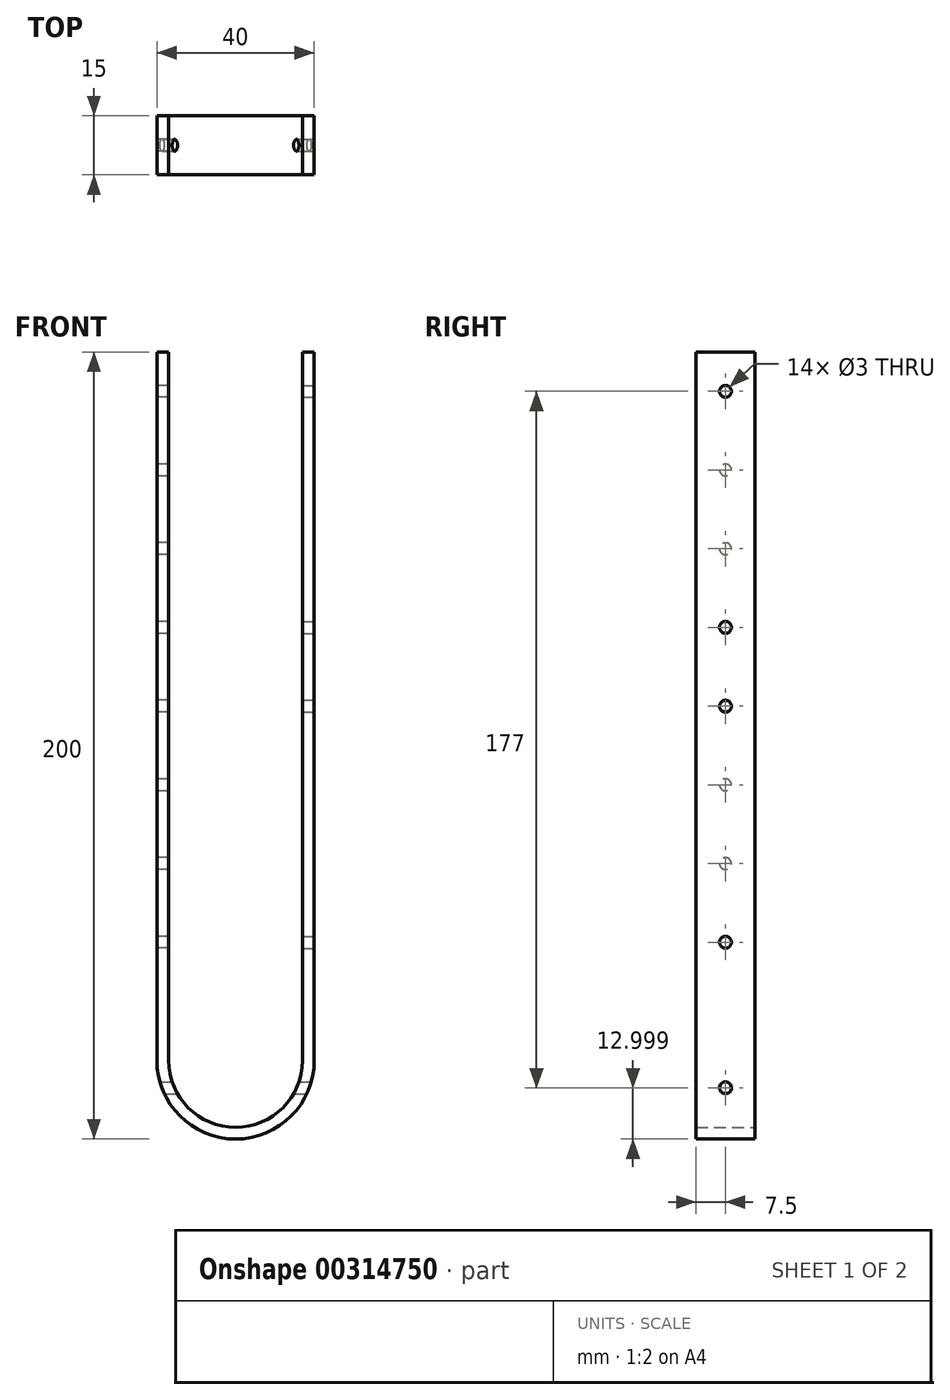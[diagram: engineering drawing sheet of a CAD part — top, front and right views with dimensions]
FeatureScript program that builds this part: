
annotation { "Feature Type Name" : "Feature", "Feature Type Description" : "" }
export const myFeature = defineFeature(function(context is Context, id is Id, definition is map)
    precondition{}
    {
        {
            var Q0;
            Q0=qCreatedBy(makeId("Front.planeOp"),FACE);
            var sketch = newSketch(context, id + "F0", { "sketchPlane" : qUnion([Q0])});
            skCircle(sketch, "E0", {"center": v(-118.34, -41.15) * mm, "radius": 20 * mm});
            skArc(sketch, "E1", {"start": v(-27.36, -89.87) * mm, "mid": v(-7.36, -109.87) * mm, "end": v(12.64, -89.87) * mm});
            skLineSegment(sketch, "E2", {"start": v(-27.36, -89.87) * mm, "end": v(-27.36, 90.13) * mm});
            skLineSegment(sketch, "E3", {"start": v(12.64, -89.87) * mm, "end": v(12.64, 90.13) * mm});
            skLineSegment(sketch, "E4.0", {"start": v(-24.36, -89.87) * mm, "end": v(-24.36, 90.13) * mm});
            skArc(sketch, "E4.1", {"start": v(-24.36, -89.87) * mm, "mid": v(-7.36, -106.87) * mm, "end": v(9.64, -89.87) * mm});
            skLineSegment(sketch, "E4.2", {"start": v(9.64, -89.87) * mm, "end": v(9.64, 90.13) * mm});
            skLineSegment(sketch, "E5", {"start": v(-27.36, 90.13) * mm, "end": v(-24.36, 90.13) * mm});
            skLineSegment(sketch, "E6", {"start": v(9.64, 90.13) * mm, "end": v(12.64, 90.13) * mm});
            skSolve(sketch);
        }
        {
            var Q0;
            Q0=makeQuery(id+"F0.imprint","IMPRINT",FACE,{"disambiguationData":[TD([[makeQuery(id+"F0.imprint","IMPRINT",EDGE,{"derivedFrom":sQuery(id+"F0.wireOp",EDGE,"E1")}),1.0]])]});
            extrude(context, id + "F1", {"entities" : qUnion([Q0]), "depth" : 15 * mm, "offsetDistance" : 25 * mm});
        }
        {
            var Q0;
            Q0=makeQuery(id+"F1.opExtrude","SWEPT_FACE",FACE,{"disambiguationData":[OSD([sQuery(id+"F0.wireOp",EDGE,"E2")])]});
            var sketch = newSketch(context, id + "F2", { "sketchPlane" : qUnion([Q0])});
            skLineSegment(sketch, "E7", {"start": v(7.5, 90.13) * mm, "end": v(7.5, 80.13) * mm});
            skCircle(sketch, "E8", {"center": v(7.5, 80.13) * mm, "radius": 1.5 * mm});
            skLineSegment(sketch, "E9", {"start": v(7.5, 80.13) * mm, "end": v(7.5, 60.13) * mm});
            skCircle(sketch, "E10", {"center": v(7.5, 60.13) * mm, "radius": 1.5 * mm});
            skLineSegment(sketch, "E11", {"start": v(7.5, 60.13) * mm, "end": v(7.5, 40.13) * mm});
            skCircle(sketch, "E12", {"center": v(7.5, 40.13) * mm, "radius": 1.5 * mm});
            skLineSegment(sketch, "E13", {"start": v(7.5, 40.13) * mm, "end": v(7.5, 90.13) * mm});
            skLineSegment(sketch, "E14.trimOffspring", {"start": v(7.5, 40.13) * mm, "end": v(7.5, 40.13) * mm});
            skPoint(sketch, "E15.start.orphan", {"position": v(7.5, -89.87) * mm});
            skLineSegment(sketch, "E16", {"start": v(7.5, 40.13) * mm, "end": v(7.5, 20.13) * mm});
            skCircle(sketch, "E17", {"center": v(7.5, 20.13) * mm, "radius": 1.35 * mm});
            skLineSegment(sketch, "E18", {"start": v(7.5, 20.13) * mm, "end": v(7.5, 0.13) * mm});
            skCircle(sketch, "E19", {"center": v(7.5, 0.13) * mm, "radius": 1.5 * mm});
            skLineSegment(sketch, "E20", {"start": v(7.5, 0.13) * mm, "end": v(7.5, -19.87) * mm});
            skCircle(sketch, "E21", {"center": v(7.5, -19.87) * mm, "radius": 1.5 * mm});
            skLineSegment(sketch, "E22", {"start": v(7.5, -19.87) * mm, "end": v(7.5, -39.87) * mm});
            skCircle(sketch, "E23", {"center": v(7.5, -39.87) * mm, "radius": 1.5 * mm});
            skLineSegment(sketch, "E24", {"start": v(7.5, -39.87) * mm, "end": v(7.5, -59.87) * mm});
            skCircle(sketch, "E25", {"center": v(7.5, -59.87) * mm, "radius": 1.5 * mm});
            skSolve(sketch);
        }
        {
            var Q0;
            Q0=sQuery(id+"F2.wireOp",VERTEX,"E9.start");
            var Q1;
            Q1=sQuery(id+"F2.wireOp",VERTEX,"E17.center");
            var Q2;
            Q2=sQuery(id+"F2.wireOp",VERTEX,"E20.start");
            var Q3;
            Q3=sQuery(id+"F2.wireOp",VERTEX,"E25.center");
            var Q4;
            Q4=sQuery(id+"F2.wireOp",VERTEX,"E11.start");
            var Q5;
            Q5=sQuery(id+"F2.wireOp",VERTEX,"E13.start");
            var Q6;
            Q6=sQuery(id+"F2.wireOp",VERTEX,"E22.start");
            var Q7;
            Q7=sQuery(id+"F2.wireOp",VERTEX,"E24.start");
            var Q8;
            Q8=makeQuery(id+"F1.opExtrude","SWEPT_BODY",BODY,{"disambiguationData":[OSD([sQuery(id+"F0.wireOp",EDGE,"E1"),sQuery(id+"F0.wireOp",EDGE,"E2"),sQuery(id+"F0.wireOp",EDGE,"E3"),sQuery(id+"F0.wireOp",EDGE,"E4.0"),sQuery(id+"F0.wireOp",EDGE,"E4.1"),sQuery(id+"F0.wireOp",EDGE,"E4.2"),sQuery(id+"F0.wireOp",EDGE,"E5"),sQuery(id+"F0.wireOp",EDGE,"E6")])]});
            hole(context, id + "F3", {"style" : HoleStyle.SIMPLE, "endStyle" : HoleEndStyle.BLIND, "holeDiameter" : 3 * mm, "holeDepth" : 10 * mm, "tappedDepth" : 12 * mm, "tapClearance" : 3, "locations" : qUnion([Q0, Q1, Q2, Q3, Q4, Q5, Q6, Q7]), "scope" : qUnion([Q8])});
        }
        {
            var Q0;
            Q0=makeQuery(id+"F1.opExtrude","SWEPT_FACE",FACE,{"disambiguationData":[OSD([sQuery(id+"F0.wireOp",EDGE,"E3")])]});
            var sketch = newSketch(context, id + "F4", { "sketchPlane" : qUnion([Q0])});
            skLineSegment(sketch, "E26", {"start": v(-7.5, 90.13) * mm, "end": v(-7.5, 80.13) * mm});
            skCircle(sketch, "E27", {"center": v(-7.5, 80.13) * mm, "radius": 1.5 * mm});
            skLineSegment(sketch, "E28", {"start": v(-7.5, 80.13) * mm, "end": v(-7.5, 20.13) * mm});
            skCircle(sketch, "E29", {"center": v(-7.5, 20.13) * mm, "radius": 1.5 * mm});
            skLineSegment(sketch, "E30", {"start": v(-7.5, 20.13) * mm, "end": v(-7.5, 0.13) * mm});
            skCircle(sketch, "E31", {"center": v(-7.5, 0.13) * mm, "radius": 1.5 * mm});
            skLineSegment(sketch, "E32", {"start": v(-7.5, 0.13) * mm, "end": v(-7.5, -59.87) * mm});
            skCircle(sketch, "E33", {"center": v(-7.5, -59.87) * mm, "radius": 1.5 * mm});
            skSolve(sketch);
        }
        {
            var Q0;
            Q0=sQuery(id+"F4.wireOp",VERTEX,"E27.center");
            var Q1;
            Q1=sQuery(id+"F4.wireOp",VERTEX,"E29.center");
            var Q2;
            Q2=sQuery(id+"F4.wireOp",VERTEX,"E31.center");
            var Q3;
            Q3=sQuery(id+"F4.wireOp",VERTEX,"E33.center");
            var Q4;
            Q4=makeQuery(id+"F1.opExtrude","SWEPT_BODY",BODY,{"disambiguationData":[OSD([sQuery(id+"F0.wireOp",EDGE,"E1"),sQuery(id+"F0.wireOp",EDGE,"E2"),sQuery(id+"F0.wireOp",EDGE,"E3"),sQuery(id+"F0.wireOp",EDGE,"E4.0"),sQuery(id+"F0.wireOp",EDGE,"E4.1"),sQuery(id+"F0.wireOp",EDGE,"E4.2"),sQuery(id+"F0.wireOp",EDGE,"E5"),sQuery(id+"F0.wireOp",EDGE,"E6")])]});
            hole(context, id + "F5", {"style" : HoleStyle.SIMPLE, "endStyle" : HoleEndStyle.BLIND, "holeDiameter" : 3 * mm, "holeDepth" : 10 * mm, "tappedDepth" : 12 * mm, "tapClearance" : 3, "locations" : qUnion([Q0, Q1, Q2, Q3]), "scope" : qUnion([Q4])});
        }
        {
            var Q0;
            Q0=makeQuery(id+"F1.opExtrude","SWEPT_FACE",FACE,{"disambiguationData":[OSD([sQuery(id+"F0.wireOp",EDGE,"E3")])]});
            var sketch = newSketch(context, id + "F6", { "sketchPlane" : qUnion([Q0])});
            skCircle(sketch, "E34", {"center": v(-7.5, -96.87) * mm, "radius": 1.5 * mm});
            skLineSegment(sketch, "E35", {"start": v(-7.5, -89.87) * mm, "end": v(-7.5, -96.87) * mm});
            skSolve(sketch);
        }
        {
            var Q0;
            Q0=sQuery(id+"F6.wireOp",VERTEX,"E34.center");
            var Q1;
            Q1=makeQuery(id+"F1.opExtrude","SWEPT_BODY",BODY,{"disambiguationData":[OSD([sQuery(id+"F0.wireOp",EDGE,"E1"),sQuery(id+"F0.wireOp",EDGE,"E2"),sQuery(id+"F0.wireOp",EDGE,"E3"),sQuery(id+"F0.wireOp",EDGE,"E4.0"),sQuery(id+"F0.wireOp",EDGE,"E4.1"),sQuery(id+"F0.wireOp",EDGE,"E4.2"),sQuery(id+"F0.wireOp",EDGE,"E5"),sQuery(id+"F0.wireOp",EDGE,"E6")])]});
            hole(context, id + "F7", {"style" : HoleStyle.SIMPLE, "endStyle" : HoleEndStyle.BLIND, "holeDiameter" : 3 * mm, "holeDepth" : 50 * mm, "tappedDepth" : 12 * mm, "tapClearance" : 3, "locations" : qUnion([Q0]), "scope" : qUnion([Q1])});
        }
    });
